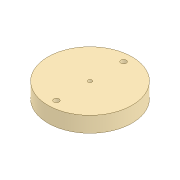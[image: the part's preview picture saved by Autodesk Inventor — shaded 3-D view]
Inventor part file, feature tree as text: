
AUTODESK INVENTOR PART (.ipt)
format: ipt  version: 2020 (Build 240168000, 168)  size: 100,864 bytes
history: native  units: mm
features: extrude x2, sketch x2, other x1, chamfer x1
ambient origin geometry x8: Origin, YZ Plane, XZ Plane, XY Plane, X Axis, Y Axis, Z Axis, Center Point
bodies: Body1 (feature_tree)
feature tree (6):
  other  "Sólido1"
  extrude  "Extrusão1"  Depth=12.0mm TaperAngle=0.0deg
  extrude  "Extrusão2"  Depth=12.0mm
  chamfer  "Chanfro1"  Distance=4.2mm
  sketch  "Esboço1"  dims[d0=65.0mm d1=12.0mm d2=0.0mm]
  sketch  "Esboço2"  dims[d3=3.0mm d4=4.2mm d5=4.2mm d6=12.0mm d7=0.0mm d8=2.5mm d9=2.0mm d10=45.0deg d11=52.0mm]
